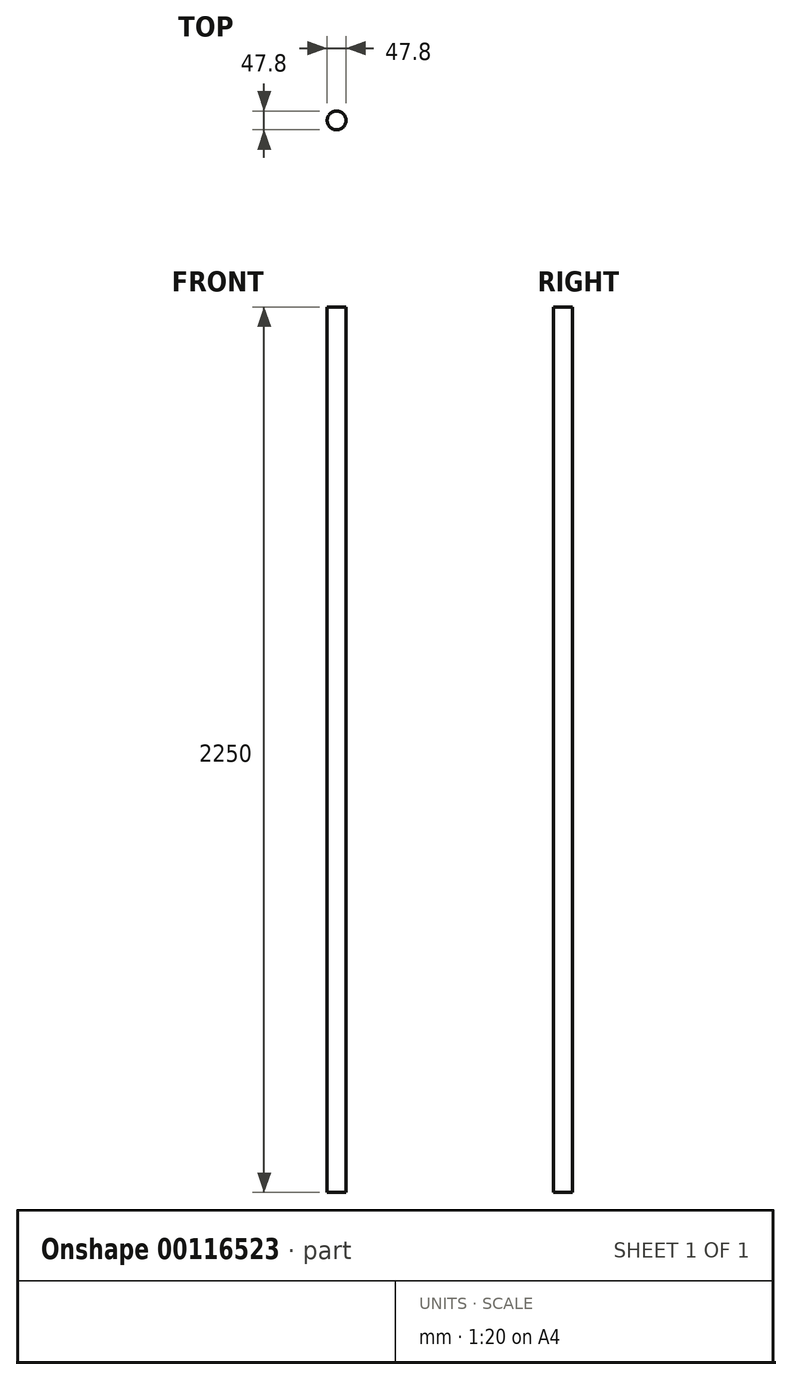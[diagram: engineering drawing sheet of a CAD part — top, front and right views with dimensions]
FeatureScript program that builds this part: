
annotation { "Feature Type Name" : "Feature", "Feature Type Description" : "" }
export const myFeature = defineFeature(function(context is Context, id is Id, definition is map)
    precondition{}
    {
        {
            var Q0;
            Q0=qCreatedBy(makeId("Top.planeOp"),FACE);
            var sketch = newSketch(context, id + "F0", { "sketchPlane" : qUnion([Q0])});
            skCircle(sketch, "E0", {"center": v(0, 0) * mm, "radius": 23.9 * mm});
            skSolve(sketch);
        }
        {
            var Q0;
            Q0=qSketchRegion(id+"F0",true);
            var Q1;
            Q1=makeQuery(id+"F0.imprint","IMPRINT",FACE,{"disambiguationData":[TD([[makeQuery(id+"F0.imprint","IMPRINT",EDGE,{"derivedFrom":sQuery(id+"F0.wireOp",EDGE,"E0")}),1.0]])]});
            extrude(context, id + "F1", {"entities" : qUnion([Q0, Q1]), "depth" : 2250 * mm});
        }
    });
